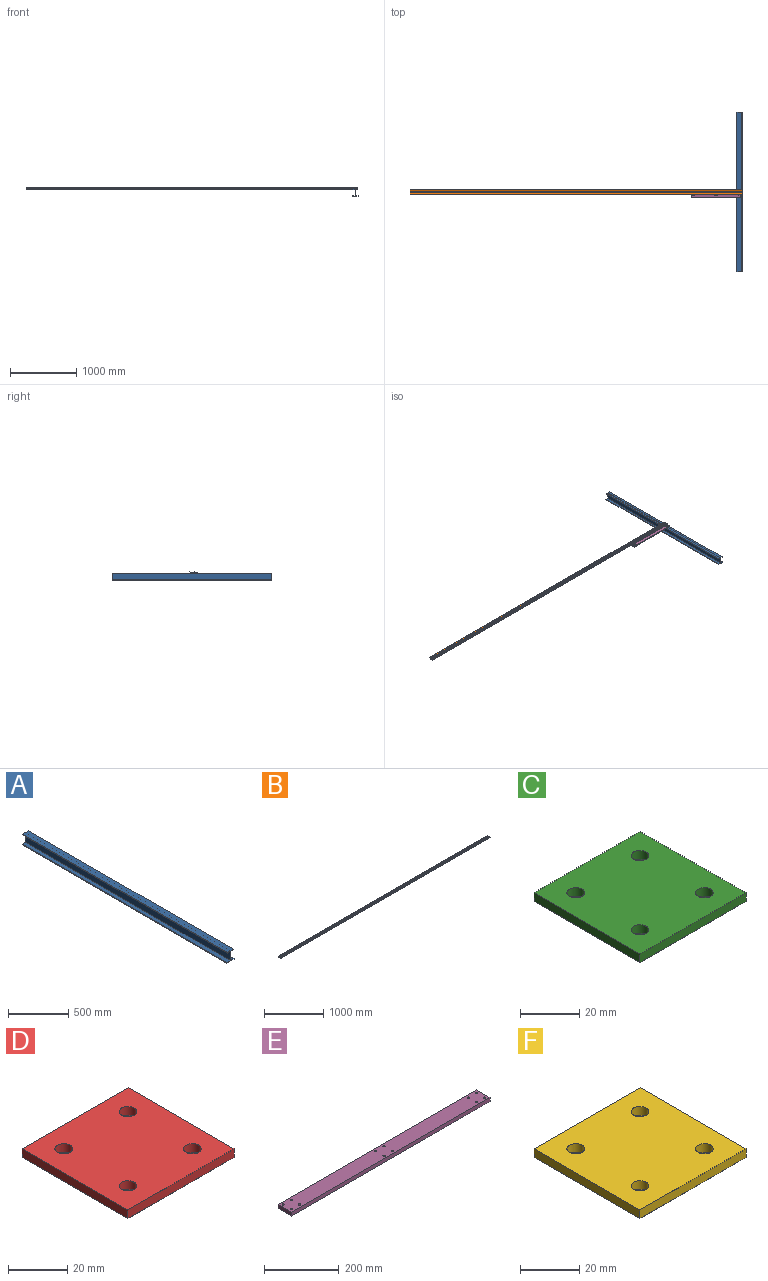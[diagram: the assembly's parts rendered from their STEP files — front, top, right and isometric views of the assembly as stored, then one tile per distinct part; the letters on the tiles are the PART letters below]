
ASSEMBLY  parts=6 mates=5
PART A: 14 faces, bbox 82.7x2400x105 mm
  f0: plane 2400x91mm, normal (1,0,0), area 218400mm2, adj f1,f11,f12,f13
  f1: plane 2400x31.85mm, normal (0,0,-1), area 76435.8mm2, adj f0,f2,f12,f13
  f2: plane 2400x6mm, normal (1,0,0), area 14400mm2, adj f1,f3,f12,f13
  f3: plane 2400x69.7mm, normal (0,0,1), area 167271.6mm2, adj f2,f4,f12,f13
  f4: plane 2400x6mm, normal (-1,0,0), area 14400mm2, adj f3,f5,f12,f13
  f5: plane 2400x31.85mm, normal (0,0,-1), area 76435.8mm2, adj f4,f6,f12,f13
  f6: plane 2400x91mm, normal (-1,0,0), area 218400mm2, adj f5,f7,f12,f13
  f7: plane 2400x38.35mm, normal (0,0,1), area 92048.6mm2, adj f6,f8,f12,f13
  f8: plane 2400x8mm, normal (-1,0,0), area 19200mm2, adj f7,f9,f12,f13
  f9: plane 2400x82.71mm, normal (0,0,-1), area 198497.2mm2, adj f8,f10,f12,f13
  f10: plane 2400x8mm, normal (1,0,0), area 19200mm2, adj f9,f11,f12,f13
  f11: plane 2400x38.35mm, normal (0,0,1), area 92048.6mm2, adj f0,f10,f12,f13
  f12: plane 105x82.71mm, normal (0,-1,0), area 1625.8mm2, adj f0,f1,f2,f3,f4,f5,f6,f7
  f13: plane 105x82.71mm, normal (0,1,0), area 1625.8mm2, adj f0,f1,f2,f3,f4,f5,f6,f7
PART B: 32 faces, bbox 5000x71.9x24.7 mm
  f0: plane 5000x33.6mm, normal (0,0,1), area 168000mm2, adj f18,f19,f20,f23
  f1: plane 5000x8.71mm, normal (0,1,0), area 43556.8mm2, adj f18,f19,f23,f24
  f2: plane 5000x9.41mm, normal (0,-0.17,-0.98), area 47804.7mm2, adj f18,f19,f24,f25
  f3: plane 5000x13.73mm, normal (0,0,-1), area 68626.5mm2, adj f18,f19,f22,f25
  f4: plane 5000x9.41mm, normal (0,0.17,-0.98), area 47804.7mm2, adj f18,f19,f21,f22
  f5: cylinder r=2.09mm len=5000mm, axis (-1,0,0), area 39476mm2, adj f6,f16,f18,f19
  f6: plane 5000x20.1mm, normal (0,-0.31,0.95), area 105782.3mm2, adj f5,f18,f19,f28
  f7: plane 5000x3.4mm, normal (0,-0.22,0.97), area 17447.2mm2, adj f18,f19,f28,f29
  f8: plane 5000x11.72mm, normal (0,0,1), area 58601.4mm2, adj f18,f19,f29,f30
  f9: plane 5000x3.4mm, normal (0,0.22,0.97), area 17447.2mm2, adj f18,f19,f30,f31
  f10: plane 5000x20.1mm, normal (0,0.31,0.95), area 105782.3mm2, adj f11,f18,f19,f31
  f11: cylinder r=2.09mm len=5000mm, axis (-1,0,0), area 39476mm2, adj f10,f12,f18,f19
  f12: plane 5000x11.13mm, normal (0,-0.31,-0.95), area 58600.2mm2, adj f11,f18,f19,f27
  f13: plane 5000x14.49mm, normal (0,-1,0), area 72456mm2, adj f14,f18,f19,f27
  f14: plane 5000x42.3mm, normal (0,0,-1), area 211500mm2, adj f13,f15,f18,f19
  f15: plane 5000x14.49mm, normal (0,1,0), area 72456mm2, adj f14,f18,f19,f26
  f16: plane 5000x11.13mm, normal (0,0.31,-0.95), area 58600.2mm2, adj f5,f18,f19,f26
  f17: plane 5000x8.71mm, normal (0,-1,0), area 43556.8mm2, adj f18,f19,f20,f21
  f18: plane 71.87x24.71mm, normal (1,0,0), area 479mm2, adj f0,f1,f2,f3,f4,f5,f6,f7
  f19: plane 71.87x24.71mm, normal (-1,0,0), area 479mm2, adj f0,f1,f2,f3,f4,f5,f6,f7
  f20: cylinder r=1.5mm len=5000mm, axis (1,0,0), area 11781mm2, adj f0,f17,f18,f19
  f21: cylinder r=1.5mm len=5000mm, axis (-1,0,0), area 13094.2mm2, adj f4,f17,f18,f19
  f22: cylinder r=1.5mm len=5000mm, axis (1,0,0), area 1313.2mm2, adj f3,f4,f18,f19
  f23: cylinder r=1.5mm len=5000mm, axis (1,0,0), area 11781mm2, adj f0,f1,f18,f19
  f24: cylinder r=1.5mm len=5000mm, axis (1,0,0), area 13094.2mm2, adj f1,f2,f18,f19
  f25: cylinder r=1.5mm len=5000mm, axis (-1,0,0), area 1313.2mm2, adj f2,f3,f18,f19
  f26: cylinder r=2.5mm len=5000mm, axis (1,0,0), area 15658.4mm2, adj f15,f16,f18,f19
  f27: cylinder r=2.5mm len=5000mm, axis (1,0,0), area 15658.4mm2, adj f12,f13,f18,f19
  f28: cylinder r=10mm len=5000mm, axis (1,0,0), area 4612.9mm2, adj f6,f7,f18,f19
  f29: cylinder r=10mm len=5000mm, axis (1,0,0), area 11293.4mm2, adj f7,f8,f18,f19
  f30: cylinder r=10mm len=5000mm, axis (-1,0,0), area 11293.4mm2, adj f8,f9,f18,f19
  f31: cylinder r=10mm len=5000mm, axis (1,0,0), area 4612.9mm2, adj f9,f10,f18,f19
PART C: 18 faces, bbox 50.8x50.8x6 mm
  f0: plane 45.8x45.8mm, normal (0,0,-1), area 1717.5mm2, adj f10,f11,f12,f13,f14,f15,f16,f17
  f1: plane 50.8x50.8mm, normal (0,0,1), area 2467.5mm2, adj f2,f3,f4,f5,f6,f7,f8,f9
  f2: plane 50.8x3.5mm, normal (0,1,0), area 177.8mm2, adj f1,f3,f5,f15
  f3: plane 50.8x3.5mm, normal (1,0,0), area 177.8mm2, adj f1,f2,f4,f14
  f4: plane 50.8x3.5mm, normal (0,-1,0), area 177.8mm2, adj f1,f3,f5,f16
  f5: plane 50.8x3.5mm, normal (-1,0,0), area 177.8mm2, adj f1,f2,f4,f17
  f6: cylinder r=3mm len=6mm, axis (0,0,1), area 66mm2, adj f1,f10
  f7: cylinder r=3mm len=6mm, axis (0,0,1), area 66mm2, adj f1,f11
  f8: cylinder r=3mm len=6mm, axis (0,0,1), area 66mm2, adj f1,f13
  f9: cylinder r=3mm len=6mm, axis (0,0,1), area 66mm2, adj f1,f12
  f10: cone r=5.5mm half-angle=45deg, axis (0,0,-1), area 94.4mm2, adj f0,f6
  f11: cone r=3mm half-angle=45deg, axis (0,0,-1), area 94.4mm2, adj f0,f7
  f12: cone r=3mm half-angle=45deg, axis (0,0,-1), area 94.4mm2, adj f0,f9
  f13: cone r=5.5mm half-angle=45deg, axis (0,0,-1), area 94.4mm2, adj f0,f8
  f14: plane 50.8x2.5mm, normal (0.71,0,-0.71), area 170.8mm2, adj f0,f3,f15,f16
  f15: plane 50.8x2.5mm, normal (0,0.71,-0.71), area 170.8mm2, adj f0,f2,f14,f17
  f16: plane 50.8x2.5mm, normal (0,-0.71,-0.71), area 170.8mm2, adj f0,f4,f14,f17
  f17: plane 50.8x2.5mm, normal (-0.71,0,-0.71), area 170.8mm2, adj f0,f5,f15,f16
PART D: 18 faces, bbox 50.8x50.8x6 mm
  f0: plane 45.8x45.8mm, normal (0,0,-1), area 1717.5mm2, adj f10,f11,f12,f13,f14,f15,f16,f17
  f1: plane 50.8x50.8mm, normal (0,0,1), area 2467.5mm2, adj f2,f3,f4,f5,f6,f7,f8,f9
  f2: plane 50.8x3.5mm, normal (0,-1,0), area 177.8mm2, adj f1,f3,f5,f15
  f3: plane 50.8x3.5mm, normal (-1,0,0), area 177.8mm2, adj f1,f2,f4,f17
  f4: plane 50.8x3.5mm, normal (0,1,0), area 177.8mm2, adj f1,f3,f5,f16
  f5: plane 50.8x3.5mm, normal (1,0,0), area 177.8mm2, adj f1,f2,f4,f14
  f6: cylinder r=3mm len=6mm, axis (0,0,1), area 66mm2, adj f1,f13
  f7: cylinder r=3mm len=6mm, axis (0,0,1), area 66mm2, adj f1,f12
  f8: cylinder r=3mm len=6mm, axis (0,0,1), area 66mm2, adj f1,f11
  f9: cylinder r=3mm len=6mm, axis (0,0,1), area 66mm2, adj f1,f10
  f10: cone r=5.5mm half-angle=45deg, axis (0,0,-1), area 94.4mm2, adj f0,f9
  f11: cone r=3mm half-angle=45deg, axis (0,0,-1), area 94.4mm2, adj f0,f8
  f12: cone r=5.5mm half-angle=45deg, axis (0,0,-1), area 94.4mm2, adj f0,f7
  f13: cone r=3mm half-angle=45deg, axis (0,0,-1), area 94.4mm2, adj f0,f6
  f14: plane 50.8x2.5mm, normal (0.71,0,-0.71), area 170.8mm2, adj f0,f5,f15,f16
  f15: plane 50.8x2.5mm, normal (0,-0.71,-0.71), area 170.8mm2, adj f0,f2,f14,f17
  f16: plane 50.8x2.5mm, normal (0,0.71,-0.71), area 170.8mm2, adj f0,f4,f14,f17
  f17: plane 50.8x2.5mm, normal (-0.71,0,-0.71), area 170.8mm2, adj f0,f3,f15,f16
PART E: 18 faces, bbox 750x50.8x12.7 mm
  f0: plane 750x50.8mm, normal (0,0,1), area 37760.7mm2, adj f2,f3,f4,f5,f6,f7,f8,f9
  f1: plane 750x50.8mm, normal (0,0,-1), area 37760.7mm2, adj f2,f3,f4,f5,f6,f7,f8,f9
  f2: plane 750x12.7mm, normal (0,-1,0), area 9525mm2, adj f0,f1,f3,f5
  f3: plane 50.8x12.7mm, normal (1,0,0), area 645.2mm2, adj f0,f1,f2,f4
  f4: plane 750x12.7mm, normal (0,1,0), area 9525mm2, adj f0,f1,f3,f5
  f5: plane 50.8x12.7mm, normal (-1,0,0), area 645.2mm2, adj f0,f1,f2,f4
  f6: cylinder r=3mm len=12.7mm, axis (0,0,1), area 239.4mm2, adj f0,f1
  f7: cylinder r=3mm len=12.7mm, axis (0,0,1), area 239.4mm2, adj f0,f1
  f8: cylinder r=3mm len=12.7mm, axis (0,0,1), area 239.4mm2, adj f0,f1
  f9: cylinder r=3mm len=12.7mm, axis (0,0,1), area 239.4mm2, adj f0,f1
  f10: cylinder r=3mm len=12.7mm, axis (0,0,1), area 239.4mm2, adj f0,f1
  f11: cylinder r=3mm len=12.7mm, axis (0,0,1), area 239.4mm2, adj f0,f1
  f12: cylinder r=3mm len=12.7mm, axis (0,0,1), area 239.4mm2, adj f0,f1
  f13: cylinder r=3mm len=12.7mm, axis (0,0,1), area 239.4mm2, adj f0,f1
  f14: cylinder r=3mm len=12.7mm, axis (0,0,1), area 239.4mm2, adj f0,f1
  f15: cylinder r=3mm len=12.7mm, axis (0,0,1), area 239.4mm2, adj f0,f1
  f16: cylinder r=3mm len=12.7mm, axis (0,0,1), area 239.4mm2, adj f0,f1
  f17: cylinder r=3mm len=12.7mm, axis (0,0,1), area 239.4mm2, adj f0,f1
PART F: 18 faces, bbox 50.8x50.8x6 mm
  f0: plane 45.8x45.8mm, normal (0,0,-1), area 1717.5mm2, adj f10,f11,f12,f13,f14,f15,f16,f17
  f1: plane 50.8x50.8mm, normal (0,0,1), area 2467.5mm2, adj f2,f3,f4,f5,f6,f7,f8,f9
  f2: plane 50.8x3.5mm, normal (1,0,0), area 177.8mm2, adj f1,f3,f5,f17
  f3: plane 50.8x3.5mm, normal (0,-1,0), area 177.8mm2, adj f1,f2,f4,f15
  f4: plane 50.8x3.5mm, normal (-1,0,0), area 177.8mm2, adj f1,f3,f5,f14
  f5: plane 50.8x3.5mm, normal (0,1,0), area 177.8mm2, adj f1,f2,f4,f16
  f6: cylinder r=3mm len=6mm, axis (0,0,1), area 66mm2, adj f1,f12
  f7: cylinder r=3mm len=6mm, axis (0,0,1), area 66mm2, adj f1,f13
  f8: cylinder r=3mm len=6mm, axis (0,0,1), area 66mm2, adj f1,f11
  f9: cylinder r=3mm len=6mm, axis (0,0,1), area 66mm2, adj f1,f10
  f10: cone r=5.5mm half-angle=45deg, axis (0,0,-1), area 94.4mm2, adj f0,f9
  f11: cone r=3mm half-angle=45deg, axis (0,0,-1), area 94.4mm2, adj f0,f8
  f12: cone r=3mm half-angle=45deg, axis (0,0,-1), area 94.4mm2, adj f0,f6
  f13: cone r=5.5mm half-angle=45deg, axis (0,0,-1), area 94.4mm2, adj f0,f7
  f14: plane 50.8x2.5mm, normal (-0.71,0,-0.71), area 170.8mm2, adj f0,f4,f15,f16
  f15: plane 50.8x2.5mm, normal (0,-0.71,-0.71), area 170.8mm2, adj f0,f3,f14,f17
  f16: plane 50.8x2.5mm, normal (0,0.71,-0.71), area 170.8mm2, adj f0,f5,f14,f17
  f17: plane 50.8x2.5mm, normal (0.71,0,-0.71), area 170.8mm2, adj f0,f2,f15,f16
PLACE A t=(0,1221.15,0)mm
PLACE B t=(-5000,21.15,0)mm
PLACE C t=(-384.45,-43.85,6)mm
PLACE D t=(-384.45,-43.85,6)mm
PLACE E t=(-384.45,-43.85,6)mm
PLACE F t=(-384.45,-43.85,6)mm
MATE fastened E.f9 <-> C.f7  axis (0,0,-1) through (-369.05,-59.25,6)mm
MATE fastened B.f14 <-> A.f3  axis (0,0,-1) through (0,21.15,0)mm
MATE fastened E.f1 <-> F.f1  axis (0,0,-1) through (-759.45,-18.45,6)mm
MATE planar A.f3 <-> D.f0  axis (0,0,1) through (-34.85,21.15,0)mm
MATE fastened E.f1 <-> D.f1  axis (0,0,-1) through (-9.45,-69.25,6)mm
